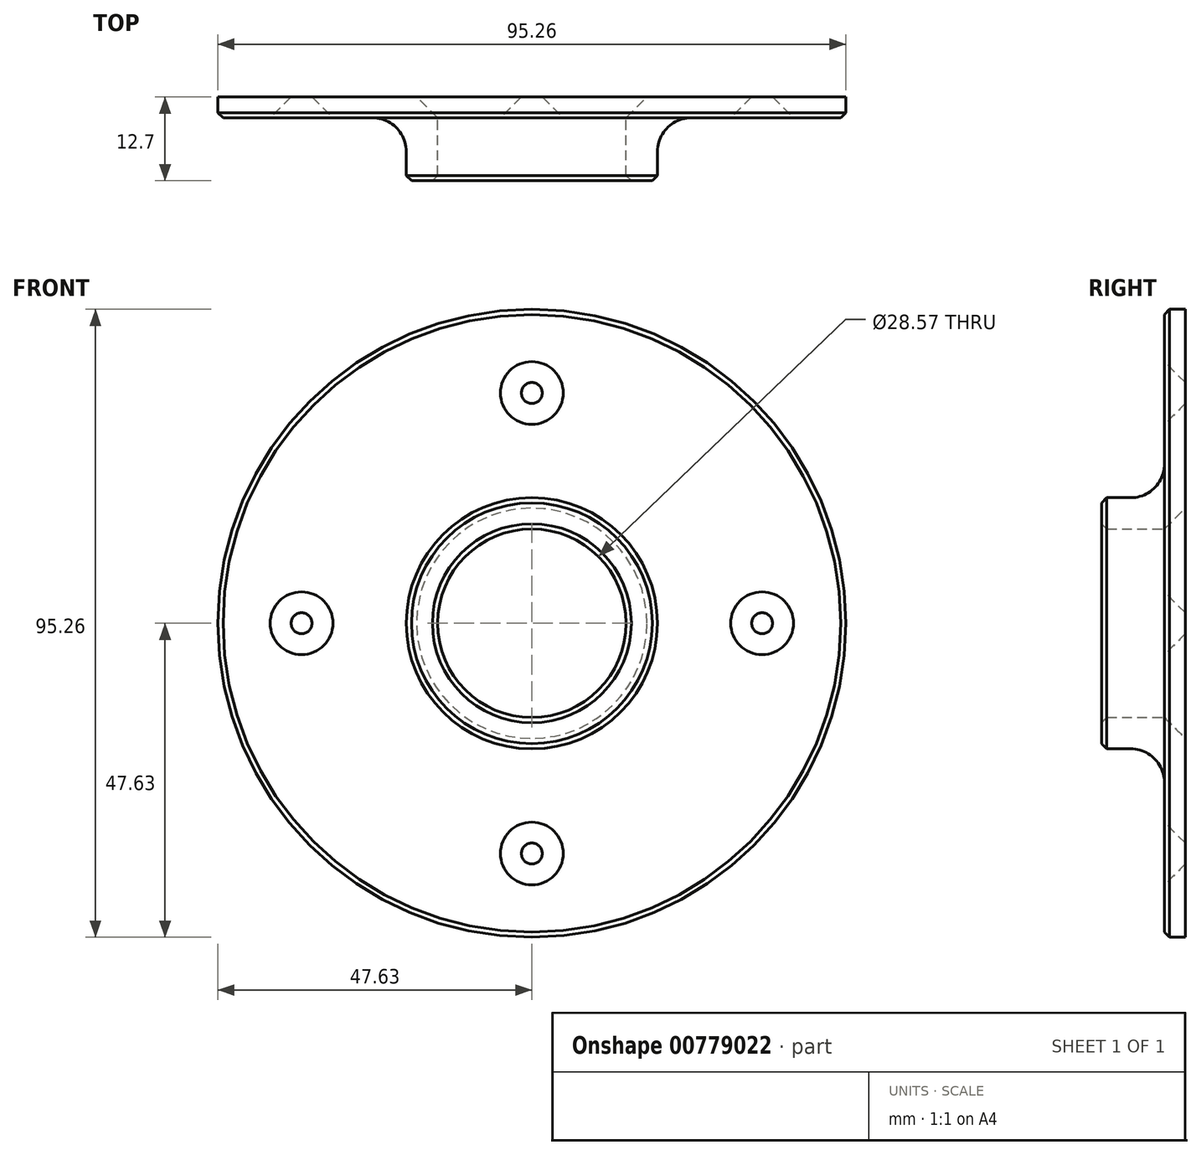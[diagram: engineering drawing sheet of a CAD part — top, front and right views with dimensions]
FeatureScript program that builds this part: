
annotation { "Feature Type Name" : "Feature", "Feature Type Description" : "" }
export const myFeature = defineFeature(function(context is Context, id is Id, definition is map)
    precondition{}
    {
        {
            var Q0;
            Q0=qCreatedBy(makeId("Front.planeOp"),FACE);
            var sketch = newSketch(context, id + "F0", { "sketchPlane" : qUnion([Q0])});
            skCircle(sketch, "E0", {"center": v(0, 0) * mm, "radius": 47.63 * mm});
            skCircle(sketch, "E1", {"center": v(0, 0) * mm, "radius": 19.05 * mm});
            skCircle(sketch, "E2", {"center": v(0, 0) * mm, "radius": 14.29 * mm});
            skCircle(sketch, "E3", {"center": v(-34.93, 0) * mm, "radius": 1.59 * mm});
            skCircle(sketch, "E4", {"center": v(34.93, 0) * mm, "radius": 1.59 * mm});
            skCircle(sketch, "E5", {"center": v(0, 34.93) * mm, "radius": 1.59 * mm});
            skCircle(sketch, "E6", {"center": v(0, -34.93) * mm, "radius": 1.59 * mm});
            skSolve(sketch);
        }
        {
            var Q0;
            Q0 = qSketchRegion(id + "F0", true);
            var Q1;
            Q1=makeQuery(id+"F0.imprint","IMPRINT",FACE,{"disambiguationData":[TD([[makeQuery(id+"F0.imprint","IMPRINT",EDGE,{"derivedFrom":sQuery(id+"F0.wireOp",EDGE,"E1")}),1.0]])]});
            extrude(context, id + "F1", {"entities" : qUnion([Q0, Q1]), "depth" : 3.17 * mm, "offsetDistance" : 25.4 * mm});
        }
        {
            var Q0;
            Q0=makeQuery(id+"F0.imprint","IMPRINT",FACE,{"disambiguationData":[TD([[makeQuery(id+"F0.imprint","IMPRINT",EDGE,{"derivedFrom":sQuery(id+"F0.wireOp",EDGE,"E1")}),1.0]])]});
            var Q1;
            Q1=sQuery(id+"F0.wireOp",EDGE,"E1");
            var Q2;
            Q2=sQuery(id+"F0.wireOp",EDGE,"E2");
            extrude(context, id + "F2", {"entities" : qUnion([Q0]), "operationType" : NewBodyOperationType.ADD, "surfaceEntities" : qUnion([Q1, Q2]), "depth" : 12.7 * mm, "offsetDistance" : 25.4 * mm});
        }
        {
            var Q0;
            Q0=makeQuery(id+"F1.opExtrude","CAP_EDGE",EDGE,{"disambiguationData":[OSD([sQuery(id+"F0.wireOp",EDGE,"E5")])],"isStart":false});
            var Q1;
            Q1=makeQuery(id+"F1.opExtrude","CAP_EDGE",EDGE,{"disambiguationData":[OSD([sQuery(id+"F0.wireOp",EDGE,"E3")])],"isStart":false});
            var Q2;
            Q2=makeQuery(id+"F1.opExtrude","CAP_EDGE",EDGE,{"disambiguationData":[OSD([sQuery(id+"F0.wireOp",EDGE,"E4")])],"isStart":false});
            var Q3;
            Q3=makeQuery(id+"F1.opExtrude","CAP_EDGE",EDGE,{"disambiguationData":[OSD([sQuery(id+"F0.wireOp",EDGE,"E6")])],"isStart":false});
            chamfer(context, id + "F3", {"entities" : qUnion([Q0, Q1, Q2, Q3]), "width" : 3.17 * mm, "tangentPropagation" : true});
        }
        {
            var Q0;
            Q0=makeQuery(id+"F1.opExtrude","CAP_EDGE",EDGE,{"disambiguationData":[OSD([sQuery(id+"F0.wireOp",EDGE,"E0")])],"isStart":false});
            chamfer(context, id + "F4", {"entities" : qUnion([Q0]), "width" : 0.8 * mm, "tangentPropagation" : true});
        }
        {
            var Q0;
            Q0=makeQuery(id+"F2.opExtrude","CAP_EDGE",EDGE,{"disambiguationData":[OSD([sQuery(id+"F0.wireOp",EDGE,"E1")])],"isStart":false});
            var Q1;
            Q1=makeQuery(id+"F2.opExtrude","CAP_EDGE",EDGE,{"disambiguationData":[OSD([sQuery(id+"F0.wireOp",EDGE,"E2")])],"isStart":false});
            chamfer(context, id + "F5", {"entities" : qUnion([Q0, Q1]), "width" : 0.8 * mm, "tangentPropagation" : true});
        }
        {
            var Q0;
            Q0=makeQuery(id+"F2.boolean.opBoolean","INTERSECT",EDGE,{"derivedFrom":[makeQuery(id+"F1.opExtrude","CAP_FACE",FACE,{"disambiguationData":[OSD([sQuery(id+"F0.wireOp",EDGE,"E0"),sQuery(id+"F0.wireOp",EDGE,"E2"),sQuery(id+"F0.wireOp",EDGE,"E3"),sQuery(id+"F0.wireOp",EDGE,"E4"),sQuery(id+"F0.wireOp",EDGE,"E5"),sQuery(id+"F0.wireOp",EDGE,"E6")])],"isStart":false}),makeQuery(id+"F2.opExtrude","SWEPT_FACE",FACE,{"disambiguationData":[OSD([sQuery(id+"F0.wireOp",EDGE,"E1")])]})]});
            fillet(context, id + "F6", {"entities" : qUnion([Q0]), "radius" : 5.08 * mm, "tangentPropagation" : true, "allowEdgeOverflow" : false});
        }
        {
            var Q0;
            Q0=makeQuery(id+"F1.opExtrude","CAP_EDGE",EDGE,{"disambiguationData":[OSD([sQuery(id+"F0.wireOp",EDGE,"E2")])],"isStart":true});
            chamfer(context, id + "F7", {"entities" : qUnion([Q0]), "width" : 3.17 * mm, "tangentPropagation" : true});
        }
    });
